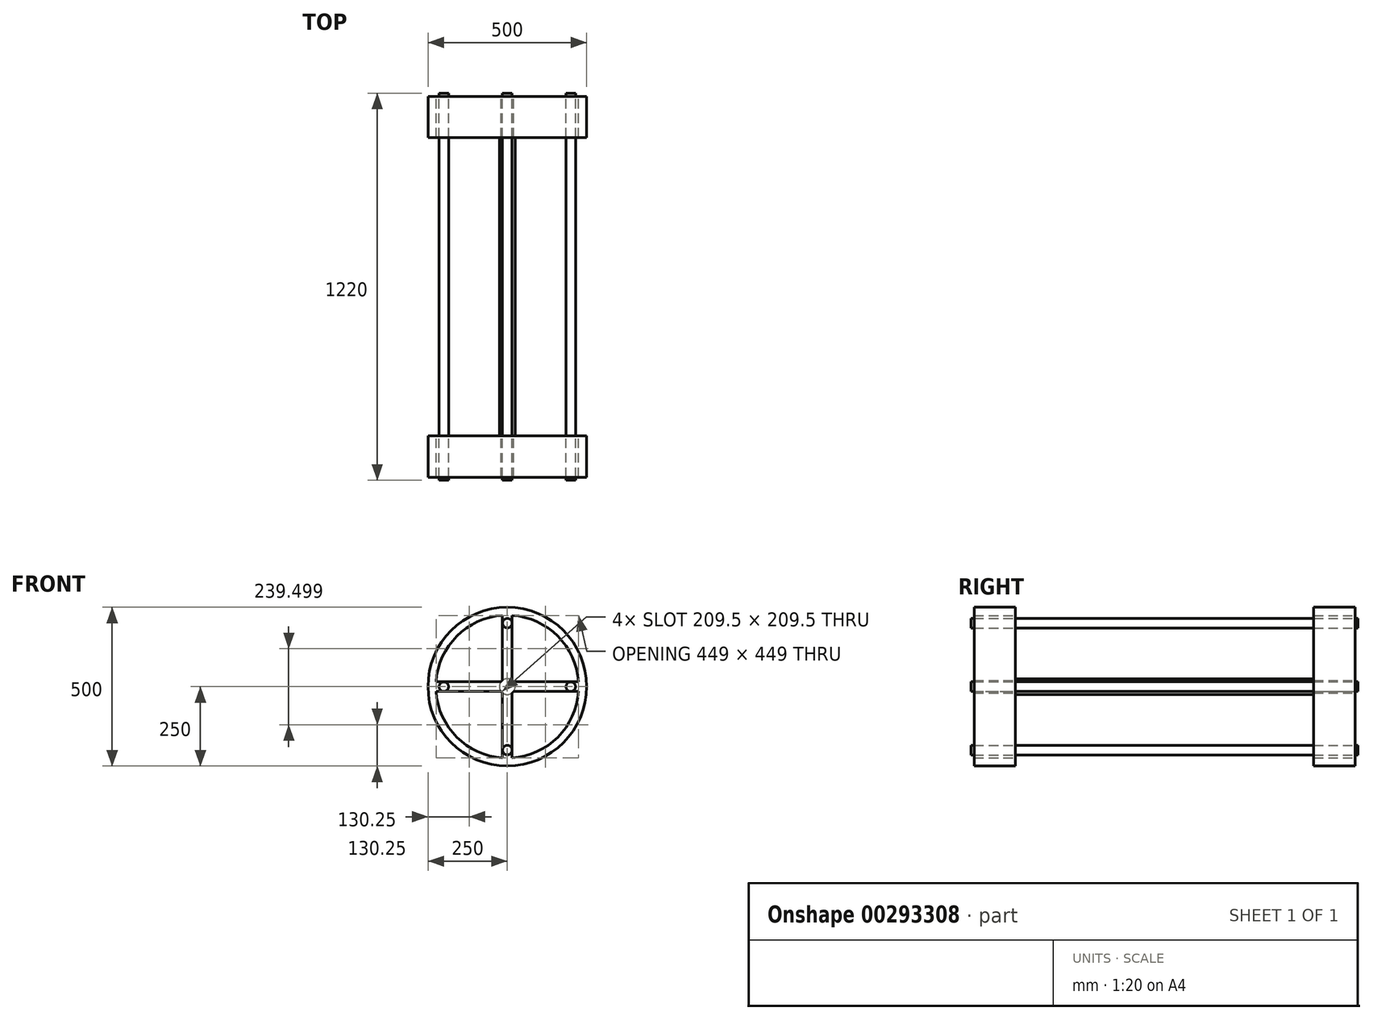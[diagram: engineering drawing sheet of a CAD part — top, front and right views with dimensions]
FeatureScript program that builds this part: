
annotation { "Feature Type Name" : "Feature", "Feature Type Description" : "" }
export const myFeature = defineFeature(function(context is Context, id is Id, definition is map)
    precondition{}
    {
        {
            var Q0;
            Q0=qCreatedBy(makeId("Front.planeOp"),FACE);
            var sketch = newSketch(context, id + "F0", { "sketchPlane" : qUnion([Q0])});
            skCircle(sketch, "E0", {"center": v(0, 0) * mm, "radius": 250 * mm});
            skSolve(sketch);
        }
        {
            var Q0;
            Q0 = qSketchRegion(id + "F0", true);
            extrude(context, id + "F1", {"entities" : qUnion([Q0]), "depth" : 600 * mm, "hasSecondDirection" : true, "secondDirectionOppositeDirection" : true, "secondDirectionDepth" : 600 * mm});
        }
        {
            var Q0;
            Q0=qCreatedBy(makeId("Front.planeOp"),FACE);
            var sketch = newSketch(context, id + "F2", { "sketchPlane" : qUnion([Q0])});
            skCircle(sketch, "E1", {"center": v(0, 0) * mm, "radius": 225 * mm});
            skCircle(sketch, "E2", {"center": v(0, 0) * mm, "radius": 25 * mm});
            skCircle(sketch, "E3", {"center": v(0, 0) * mm, "radius": 15 * mm});
            skLineSegment(sketch, "E4.left", {"start": v(-15, 224.5) * mm, "end": v(-15, 20) * mm});
            skLineSegment(sketch, "E4.right", {"start": v(15, 224.5) * mm, "end": v(15, 20) * mm});
            skLineSegment(sketch, "E5", {"start": v(0, 225) * mm, "end": v(0, 25) * mm, "construction": true});
            skLineSegment(sketch, "E6.left", {"start": v(-15, -224.5) * mm, "end": v(-15, -20) * mm});
            skLineSegment(sketch, "E6.right", {"start": v(15, -224.5) * mm, "end": v(15, -20) * mm});
            skLineSegment(sketch, "E7", {"start": v(0, -25) * mm, "end": v(0, -224.5) * mm, "construction": true});
            skLineSegment(sketch, "E8.bottom", {"start": v(-20, -15) * mm, "end": v(-224.5, -15) * mm});
            skLineSegment(sketch, "E8.top", {"start": v(-20, 15) * mm, "end": v(-224.5, 15) * mm});
            skLineSegment(sketch, "E9.bottom", {"start": v(20, -15) * mm, "end": v(224.5, -15) * mm});
            skLineSegment(sketch, "E9.top", {"start": v(20, 15) * mm, "end": v(224.5, 15) * mm});
            skLineSegment(sketch, "E10", {"start": v(-25, 0) * mm, "end": v(-224.5, 0) * mm, "construction": true});
            skLineSegment(sketch, "E11", {"start": v(0, 0) * mm, "end": v(224.5, 0) * mm, "construction": true});
            skSolve(sketch);
        }
        {
            var Q0;
            {var subQ0=sQuery(id+"F2.wireOp",EDGE,"E4.right");Q0=makeQuery(id+"F2.imprint","IMPRINT",FACE,{"disambiguationData":[TD([[makeQuery(id+"F2.imprint","IMPRINT",EDGE,{"derivedFrom":subQ0}),1.0]])]});}
            var Q1;
            {var subQ0=sQuery(id+"F2.wireOp",EDGE,"E4.left");Q1=makeQuery(id+"F2.imprint","IMPRINT",FACE,{"disambiguationData":[TD([[makeQuery(id+"F2.imprint","IMPRINT",EDGE,{"derivedFrom":subQ0}),-1.0]])]});}
            var Q2;
            {var subQ0=sQuery(id+"F2.wireOp",EDGE,"E6.left");Q2=makeQuery(id+"F2.imprint","IMPRINT",FACE,{"disambiguationData":[TD([[makeQuery(id+"F2.imprint","IMPRINT",EDGE,{"derivedFrom":subQ0}),1.0]])]});}
            var Q3;
            {var subQ0=sQuery(id+"F2.wireOp",EDGE,"E6.right");Q3=makeQuery(id+"F2.imprint","IMPRINT",FACE,{"disambiguationData":[TD([[makeQuery(id+"F2.imprint","IMPRINT",EDGE,{"derivedFrom":subQ0}),-1.0]])]});}
            extrude(context, id + "F3", {"entities" : qUnion([Q0, Q1, Q2, Q3]), "operationType" : NewBodyOperationType.REMOVE, "endBound" : BoundingType.THROUGH_ALL, "depth" : 470 * mm, "hasSecondDirection" : true, "secondDirectionBound" : SecondDirectionBoundingType.THROUGH_ALL, "secondDirectionOppositeDirection" : true, "secondDirectionDepth" : 470 * mm});
        }
        {
            var Q0;
            Q0=qCreatedBy(makeId("Front.planeOp"),FACE);
            var sketch = newSketch(context, id + "F4", { "sketchPlane" : qUnion([Q0])});
            skCircle(sketch, "E12", {"center": v(0, 0) * mm, "radius": 250 * mm});
            skCircle(sketch, "E13", {"center": v(0, 0) * mm, "radius": 25 * mm});
            skSolve(sketch);
        }
        {
            var Q0;
            Q0 = qSketchRegion(id + "F4", true);
            extrude(context, id + "F5", {"entities" : qUnion([Q0]), "operationType" : NewBodyOperationType.REMOVE, "oppositeDirection" : true, "depth" : 470 * mm, "hasSecondDirection" : true, "secondDirectionOppositeDirection" : false, "secondDirectionDepth" : 470 * mm});
        }
        {
            var Q0;
            Q0=qCreatedBy(makeId("Front.planeOp"),FACE);
            var sketch = newSketch(context, id + "F6", { "sketchPlane" : qUnion([Q0])});
            skCircle(sketch, "E14", {"center": v(0, 200) * mm, "radius": 15 * mm});
            skCircle(sketch, "E15.1.0", {"center": v(-200, 0) * mm, "radius": 15 * mm});
            skCircle(sketch, "E15.2.0", {"center": v(0, -200) * mm, "radius": 15 * mm});
            skCircle(sketch, "E15.3.0", {"center": v(200, 0) * mm, "radius": 15 * mm});
            skPoint(sketch, "E15.center", {"position": v(0, 0) * mm});
            skSolve(sketch);
        }
        {
            var Q0;
            Q0 = qSketchRegion(id + "F6", true);
            extrude(context, id + "F7", {"entities" : qUnion([Q0]), "depth" : 610 * mm, "hasSecondDirection" : true, "secondDirectionOppositeDirection" : true, "secondDirectionDepth" : 610 * mm});
        }
    });
